# Revit family: HL_Вентиляционный клапан_HL901
name_source: partatom
category: Příslušenství trubek
revit_build: Autodesk Revit 2016 (Build: 20161004_0715(x64)
units: mm (PartAtom-declared; Revit-internal decimal feet)

## family parameters
Kóta kulaté spojky = Použít průměr
Nadpis OmniClass = Liquid Waste Collection and Removal
Ořezat dutým tvarem při načtení = Ne
Sdílené = Ne
Typ součásti = Ventil – zalomení do
Vždy vertikální = Ano
Založené na pracovní rovině = Ne
Číslo OmniClass = 23.70.50.21

## types (1)
- HL_Вентиляционный клапан_HL901
    Cena = 0 $
    EAN = 9003076031269
    Klíčová poznámka = HL901
    Komentáře k typům = Вентиляционный клапан DN75/90/110 с двойной теплоизолированной стенкой и многоязычковой уплотнительной прокладкой
    Model = HL901
    Popis = Вентиляционный клапан
    URL = http://www.hutterer-lechner.com
    Výrobce = HL Hutterer & Lechner GmbH
    ВЕС = 0,362 kg
    МАТЕРИАЛ = ABS/ PP
    ПРОИЗВОДИТЕЛЬНОСТЬ = 32 l/s
    ПРОПУСКНАЯ СПОСОБНОСТЬ = 0.0 m³/h
    РАЗМЕР = DN75/90/110
    материал = Plactic - White
    материал 2 = Plastic - Blue
    материал 3 = Plactic - Black
